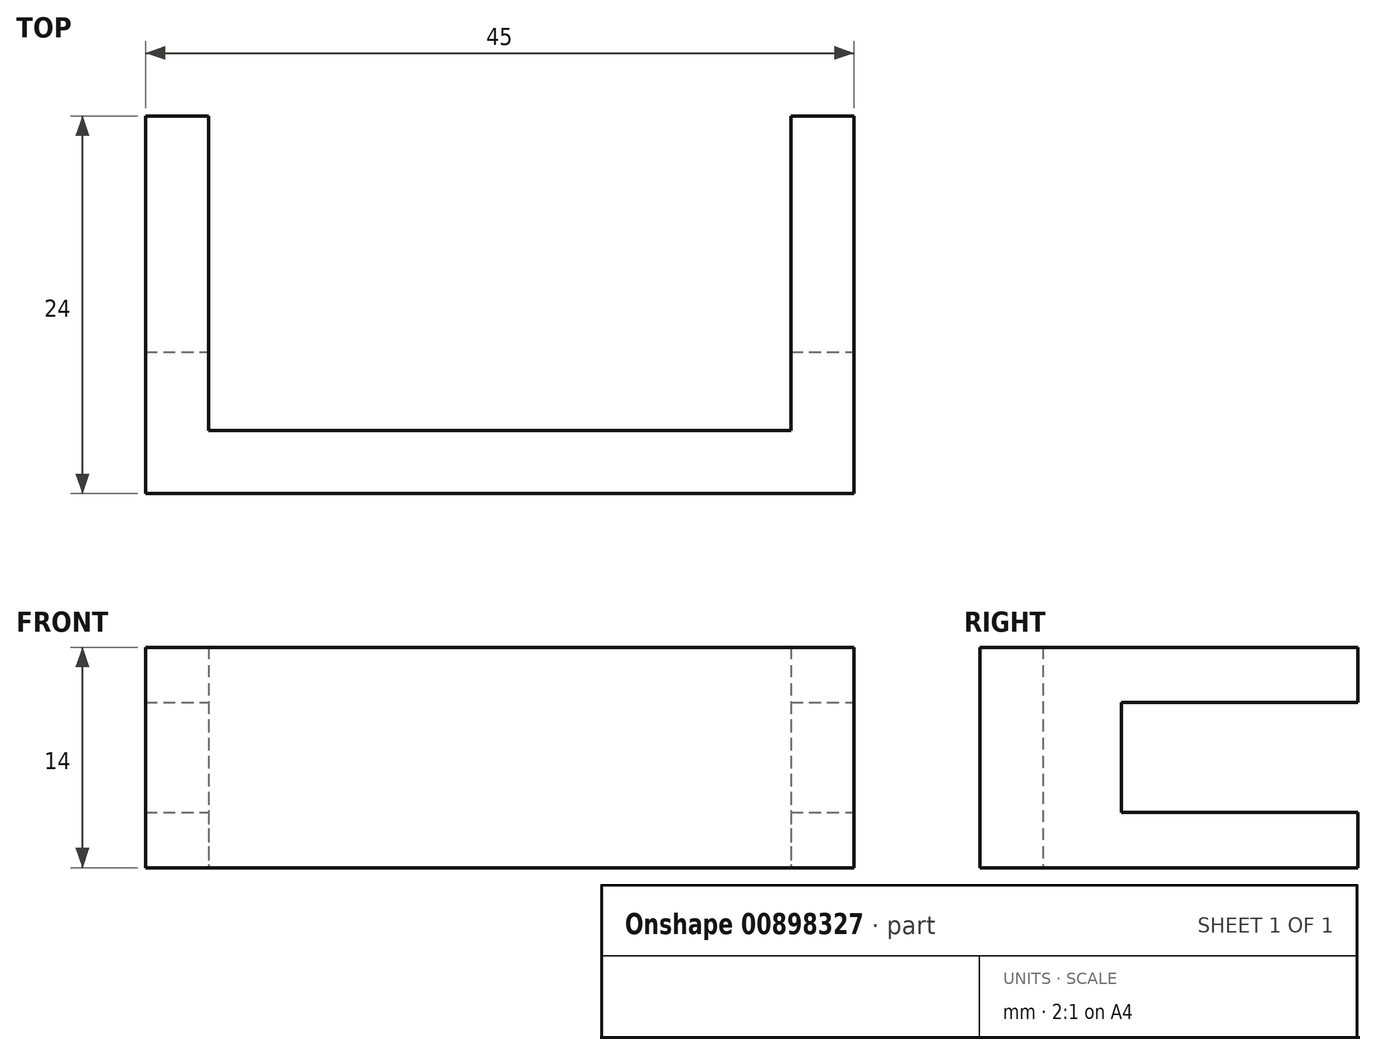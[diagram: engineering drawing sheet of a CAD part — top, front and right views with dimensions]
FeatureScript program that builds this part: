
annotation { "Feature Type Name" : "Feature", "Feature Type Description" : "" }
export const myFeature = defineFeature(function(context is Context, id is Id, definition is map)
    precondition{}
    {
        {
            var Q0;
            Q0=qCreatedBy(makeId("Top.planeOp"),FACE);
            var sketch = newSketch(context, id + "F0", { "sketchPlane" : qUnion([Q0])});
            skLineSegment(sketch, "E0", {"start": v(0, 0) * mm, "end": v(18.5, 0) * mm});
            skLineSegment(sketch, "E1", {"start": v(22.5, -4) * mm, "end": v(0, -4) * mm});
            skLineSegment(sketch, "E2.MirrorCS", {"start": v(-22.5, -4) * mm, "end": v(0, -4) * mm});
            skLineSegment(sketch, "E3.MirrorCS", {"start": v(0, 0) * mm, "end": v(-18.5, 0) * mm});
            skLineSegment(sketch, "E4", {"start": v(18.5, 20) * mm, "end": v(22.5, 20) * mm});
            skLineSegment(sketch, "E5", {"start": v(18.5, 0) * mm, "end": v(18.5, 20) * mm});
            skLineSegment(sketch, "E6", {"start": v(22.5, 20) * mm, "end": v(22.5, -4) * mm});
            skLineSegment(sketch, "E7.MirrorCS", {"start": v(-18.5, 0) * mm, "end": v(-18.5, 20) * mm});
            skLineSegment(sketch, "E8.MirrorCS", {"start": v(-22.5, 20) * mm, "end": v(-22.5, -4) * mm});
            skLineSegment(sketch, "E9.MirrorCS", {"start": v(-18.5, 20) * mm, "end": v(-22.5, 20) * mm});
            skSolve(sketch);
        }
        {
            var Q0;
            Q0=makeQuery(id+"F0.imprint","IMPRINT",FACE,{"disambiguationData":[TD([[makeQuery(id+"F0.imprint","IMPRINT",EDGE,{"derivedFrom":sQuery(id+"F0.wireOp",EDGE,"E0")}),-1.0]])]});
            extrude(context, id + "F1", {"entities" : qUnion([Q0]), "depth" : 14 * mm, "offsetDistance" : 25 * mm});
        }
        {
            var Q0;
            Q0=makeQuery(id+"F1.opExtrude","SWEPT_FACE",FACE,{"disambiguationData":[OSD([sQuery(id+"F0.wireOp",EDGE,"E6")])]});
            var sketch = newSketch(context, id + "F2", { "sketchPlane" : qUnion([Q0])});
            skLineSegment(sketch, "E10", {"start": v(20, 7) * mm, "end": v(20, 10.5) * mm});
            skLineSegment(sketch, "E11", {"start": v(20, 7) * mm, "end": v(20, 3.5) * mm});
            skLineSegment(sketch, "E12", {"start": v(20, 3.5) * mm, "end": v(5, 3.5) * mm});
            skLineSegment(sketch, "E13", {"start": v(5, 3.5) * mm, "end": v(5, 10.5) * mm});
            skLineSegment(sketch, "E14", {"start": v(5, 10.5) * mm, "end": v(20, 10.5) * mm});
            skSolve(sketch);
        }
        {
            var Q0;
            Q0=makeQuery(id+"F2.imprint","IMPRINT",FACE,{"disambiguationData":[TD([[makeQuery(id+"F2.imprint","IMPRINT",EDGE,{"derivedFrom":sQuery(id+"F2.wireOp",EDGE,"E10")}),-1.0]])]});
            extrude(context, id + "F3", {"entities" : qUnion([Q0]), "operationType" : NewBodyOperationType.REMOVE, "oppositeDirection" : true, "depth" : 100 * mm, "offsetDistance" : 25 * mm});
        }
    });
